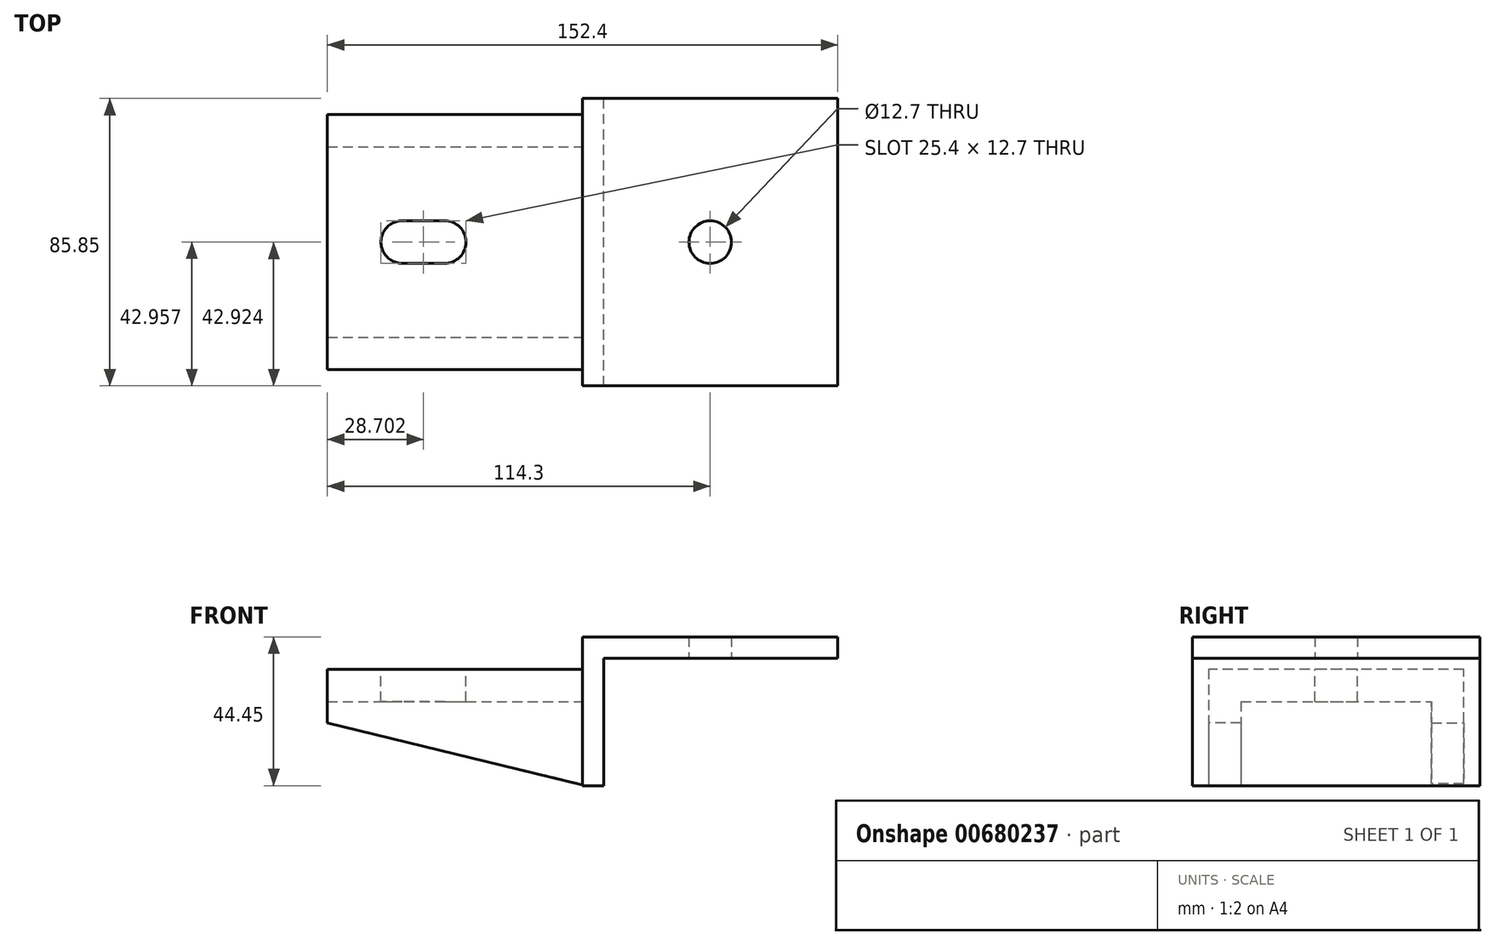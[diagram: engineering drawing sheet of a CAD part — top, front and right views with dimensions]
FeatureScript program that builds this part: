
annotation { "Feature Type Name" : "Feature", "Feature Type Description" : "" }
export const myFeature = defineFeature(function(context is Context, id is Id, definition is map)
    precondition{}
    {
        {
            var Q0;
            Q0=qCreatedBy(makeId("Top.planeOp"),FACE);
            var sketch = newSketch(context, id + "F0", { "sketchPlane" : qUnion([Q0])});
            skLineSegment(sketch, "E0.bottom", {"start": v(0, 0) * mm, "end": v(-76.2, 0) * mm});
            skLineSegment(sketch, "E0.top", {"start": v(0, -85.85) * mm, "end": v(-76.2, -85.85) * mm});
            skLineSegment(sketch, "E0.left", {"start": v(0, 0) * mm, "end": v(0, -85.85) * mm});
            skLineSegment(sketch, "E0.right", {"start": v(-76.2, 0) * mm, "end": v(-76.2, -85.85) * mm});
            skLineSegment(sketch, "E1", {"start": v(-76.2, 0) * mm, "end": v(-38.1, 0) * mm});
            skLineSegment(sketch, "E2", {"start": v(-38.1, 0) * mm, "end": v(-38.1, -42.93) * mm, "construction": true});
            skCircle(sketch, "E3", {"center": v(-38.1, -42.93) * mm, "radius": 6.35 * mm});
            skSolve(sketch);
        }
        {
            var Q0;
            Q0 = qSketchRegion(id + "F0", true);
            extrude(context, id + "F1", {"entities" : qUnion([Q0]), "depth" : 6.35 * mm, "offsetDistance" : 25.4 * mm});
        }
        {
            var Q0;
            Q0=makeQuery(id+"F1.opExtrude","CAP_FACE",FACE,{"disambiguationData":[OSD([sQuery(id+"F0.wireOp",EDGE,"E0.bottom"),sQuery(id+"F0.wireOp",EDGE,"E0.top"),sQuery(id+"F0.wireOp",EDGE,"E0.left"),sQuery(id+"F0.wireOp",EDGE,"E0.right"),sQuery(id+"F0.wireOp",EDGE,"E3")])],"isStart":true});
            var sketch = newSketch(context, id + "F2", { "sketchPlane" : qUnion([Q0])});
            skLineSegment(sketch, "E4", {"start": v(-76.2, 85.85) * mm, "end": v(-69.85, 85.85) * mm});
            skLineSegment(sketch, "E5", {"start": v(-69.85, 85.85) * mm, "end": v(-69.85, 0) * mm});
            skLineSegment(sketch, "E6", {"start": v(-69.85, 0) * mm, "end": v(-76.2, 0) * mm});
            skLineSegment(sketch, "E7", {"start": v(-76.2, 0) * mm, "end": v(-76.2, 85.85) * mm});
            skSolve(sketch);
        }
        {
            var Q0;
            Q0=makeQuery(id+"F2.imprint","IMPRINT",FACE,{"disambiguationData":[TD([[makeQuery(id+"F2.imprint","IMPRINT",EDGE,{"derivedFrom":sQuery(id+"F2.wireOp",EDGE,"E4")}),1.0]])]});
            extrude(context, id + "F3", {"entities" : qUnion([Q0]), "operationType" : NewBodyOperationType.ADD, "depth" : 38.1 * mm, "offsetDistance" : 25.4 * mm});
        }
        {
            var Q0;
            Q0=makeQuery(id+"F3.boolean.opBoolean","MERGE",FACE,{"derivedFrom":[makeQuery(id+"F1.opExtrude","SWEPT_FACE",FACE,{"disambiguationData":[OSD([sQuery(id+"F0.wireOp",EDGE,"E0.right")])]}),makeQuery(id+"F3.opExtrude","SWEPT_FACE",FACE,{"disambiguationData":[OSD([sQuery(id+"F2.wireOp",EDGE,"E7")])]})]});
            var sketch = newSketch(context, id + "F4", { "sketchPlane" : qUnion([Q0])});
            skLineSegment(sketch, "E8", {"start": v(0, 6.35) * mm, "end": v(4.83, 6.35) * mm, "construction": true});
            skLineSegment(sketch, "E9", {"start": v(4.83, 6.35) * mm, "end": v(4.83, -3.3) * mm, "construction": true});
            skLineSegment(sketch, "E10", {"start": v(4.83, -3.3) * mm, "end": v(81.03, -3.3) * mm});
            skLineSegment(sketch, "E11", {"start": v(81.03, -3.3) * mm, "end": v(81.03, -12.95) * mm});
            skLineSegment(sketch, "E12", {"start": v(81.03, -12.95) * mm, "end": v(4.83, -12.95) * mm});
            skLineSegment(sketch, "E13", {"start": v(4.83, -12.95) * mm, "end": v(4.83, -3.3) * mm});
            skSolve(sketch);
        }
        {
            var Q0;
            Q0=makeQuery(id+"F4.imprint","IMPRINT",FACE,{"disambiguationData":[TD([[makeQuery(id+"F4.imprint","IMPRINT",EDGE,{"derivedFrom":sQuery(id+"F4.wireOp",EDGE,"E10")}),-1.0]])]});
            extrude(context, id + "F5", {"entities" : qUnion([Q0]), "operationType" : NewBodyOperationType.ADD, "depth" : 76.2 * mm, "offsetDistance" : 25.4 * mm});
        }
        {
            var Q0;
            Q0=makeQuery(id+"F5.opExtrude","SWEPT_FACE",FACE,{"disambiguationData":[OSD([sQuery(id+"F4.wireOp",EDGE,"E10")])]});
            var sketch = newSketch(context, id + "F6", { "sketchPlane" : qUnion([Q0])});
            skLineSegment(sketch, "E14", {"start": v(-76.2, -42.9) * mm, "end": v(-117.35, -42.9) * mm, "construction": true});
            skCircle(sketch, "E15", {"center": v(-117.35, -42.9) * mm, "radius": 6.35 * mm});
            skLineSegment(sketch, "E16", {"start": v(-117.35, -42.9) * mm, "end": v(-130.05, -42.9) * mm, "construction": true});
            skCircle(sketch, "E17", {"center": v(-130.05, -42.9) * mm, "radius": 6.35 * mm});
            skLineSegment(sketch, "E18", {"start": v(-130.04, -36.54) * mm, "end": v(-117.35, -36.54) * mm});
            skLineSegment(sketch, "E19", {"start": v(-130.04, -49.24) * mm, "end": v(-117.35, -49.24) * mm});
            skSolve(sketch);
        }
        {
            var Q0;
            {var subQ0=sQuery(id+"F6.wireOp",EDGE,"E17");var subQ1=makeQuery(id+"F6.imprint","INTERSECT",VERTEX,{"derivedFrom":[subQ0,sQuery(id+"F6.wireOp",EDGE,"E18")]});Q0=makeQuery(id+"F6.imprint","IMPRINT",FACE,{"disambiguationData":[TD([[makeQuery(id+"F6.imprint","IMPRINT",EDGE,{"disambiguationData":[TD([[subQ1,1.0]])],"derivedFrom":subQ0}),1.0]])]});}
            var Q1;
            {var subQ0=sQuery(id+"F6.wireOp",EDGE,"E18");Q1=makeQuery(id+"F6.imprint","IMPRINT",FACE,{"disambiguationData":[TD([[makeQuery(id+"F6.imprint","IMPRINT",EDGE,{"derivedFrom":subQ0}),-1.0]])]});}
            var Q2;
            {var subQ0=sQuery(id+"F6.wireOp",EDGE,"E15");var subQ1=makeQuery(id+"F6.imprint","INTERSECT",VERTEX,{"derivedFrom":[subQ0,sQuery(id+"F6.wireOp",EDGE,"E18")]});Q2=makeQuery(id+"F6.imprint","IMPRINT",FACE,{"disambiguationData":[TD([[makeQuery(id+"F6.imprint","IMPRINT",EDGE,{"disambiguationData":[TD([[subQ1,-1.0]])],"derivedFrom":subQ0}),1.0]])]});}
            var Q3;
            {var subQ0=sQuery(id+"F6.wireOp",EDGE,"E19");Q3=makeQuery(id+"F6.imprint","IMPRINT",FACE,{"disambiguationData":[TD([[makeQuery(id+"F6.imprint","IMPRINT",EDGE,{"derivedFrom":subQ0}),1.0]])]});}
            extrude(context, id + "F7", {"entities" : qUnion([Q0, Q1, Q2, Q3]), "operationType" : NewBodyOperationType.REMOVE, "oppositeDirection" : true, "depth" : 10.16 * mm, "offsetDistance" : 25.4 * mm});
        }
        {
            var Q0;
            Q0=makeQuery(id+"F5.opExtrude","SWEPT_FACE",FACE,{"disambiguationData":[OSD([sQuery(id+"F4.wireOp",EDGE,"E11")])]});
            var sketch = newSketch(context, id + "F8", { "sketchPlane" : qUnion([Q0])});
            skLineSegment(sketch, "E20", {"start": v(-152.4, -12.95) * mm, "end": v(-152.4, -19.3) * mm});
            skLineSegment(sketch, "E21", {"start": v(-152.4, -19.3) * mm, "end": v(-75.78, -37.93) * mm});
            skLineSegment(sketch, "E22", {"start": v(-75.78, -37.93) * mm, "end": v(-76.2, -12.95) * mm});
            skLineSegment(sketch, "E23", {"start": v(-76.2, -12.95) * mm, "end": v(-152.4, -12.95) * mm});
            skSolve(sketch);
        }
        {
            var Q0;
            Q0=makeQuery(id+"F8.imprint","IMPRINT",FACE,{"disambiguationData":[TD([[makeQuery(id+"F8.imprint","IMPRINT",EDGE,{"derivedFrom":sQuery(id+"F8.wireOp",EDGE,"E20")}),1.0]])]});
            extrude(context, id + "F9", {"entities" : qUnion([Q0]), "operationType" : NewBodyOperationType.ADD, "oppositeDirection" : true, "depth" : 9.65 * mm, "offsetDistance" : 25.4 * mm});
        }
        {
            var Q0;
            Q0=makeQuery(id+"F5.opExtrude","SWEPT_FACE",FACE,{"disambiguationData":[OSD([sQuery(id+"F4.wireOp",EDGE,"E13")])]});
            var sketch = newSketch(context, id + "F10", { "sketchPlane" : qUnion([Q0])});
            skLineSegment(sketch, "E24", {"start": v(152.4, -12.95) * mm, "end": v(152.4, -19.3) * mm});
            skLineSegment(sketch, "E25", {"start": v(152.4, -19.3) * mm, "end": v(75.94, -37.61) * mm});
            skLineSegment(sketch, "E26", {"start": v(75.94, -37.61) * mm, "end": v(76.2, -12.95) * mm});
            skLineSegment(sketch, "E27", {"start": v(76.2, -12.95) * mm, "end": v(152.4, -12.95) * mm});
            skSolve(sketch);
        }
        {
            var Q0;
            Q0=makeQuery(id+"F10.imprint","IMPRINT",FACE,{"disambiguationData":[TD([[makeQuery(id+"F10.imprint","IMPRINT",EDGE,{"derivedFrom":sQuery(id+"F10.wireOp",EDGE,"E24")}),-1.0]])]});
            extrude(context, id + "F11", {"entities" : qUnion([Q0]), "operationType" : NewBodyOperationType.ADD, "oppositeDirection" : true, "depth" : 9.65 * mm, "offsetDistance" : 25.4 * mm});
        }
    });
